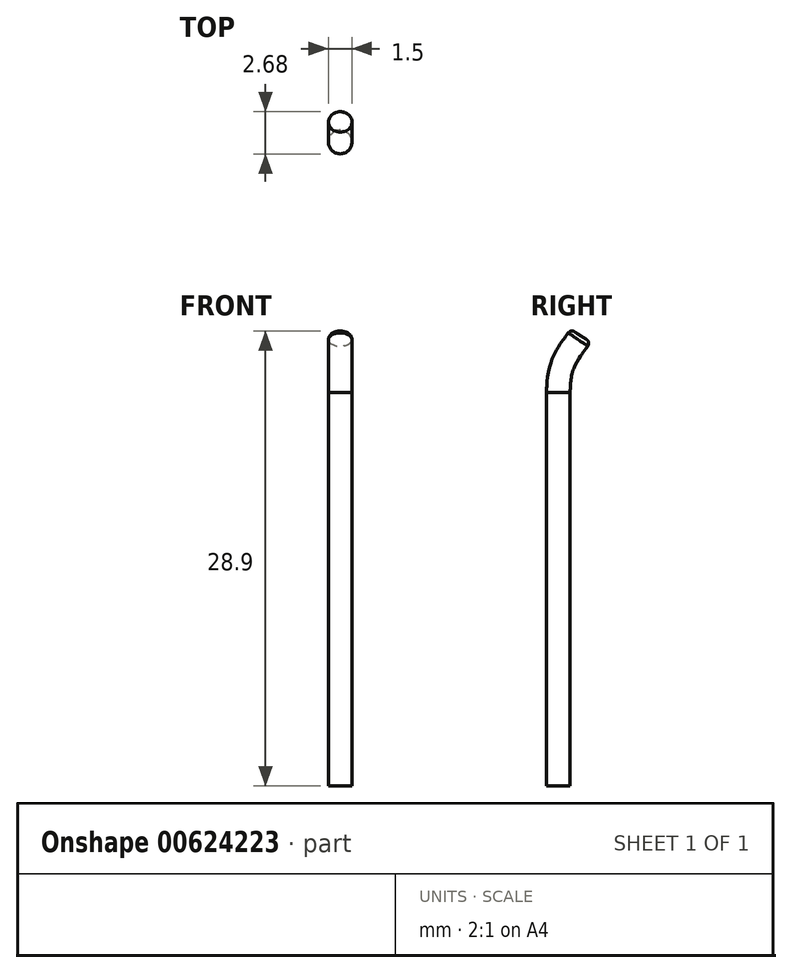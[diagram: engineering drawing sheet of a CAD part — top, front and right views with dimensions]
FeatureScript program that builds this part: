
annotation { "Feature Type Name" : "Feature", "Feature Type Description" : "" }
export const myFeature = defineFeature(function(context is Context, id is Id, definition is map)
    precondition{}
    {
        {
            var Q0;
            Q0=qCreatedBy(makeId("Top.planeOp"),FACE);
            var sketch = newSketch(context, id + "F0", { "sketchPlane" : qUnion([Q0])});
            skCircle(sketch, "E0", {"center": v(0, 0) * mm, "radius": 0.75 * mm});
            skSolve(sketch);
        }
        {
            var Q0;
            Q0=makeQuery(id+"F0.imprint","IMPRINT",FACE,{"disambiguationData":[TD([[makeQuery(id+"F0.imprint","IMPRINT",EDGE,{"derivedFrom":sQuery(id+"F0.wireOp",EDGE,"E0")}),1.0]])]});
            extrude(context, id + "F1", {"entities" : qUnion([Q0]), "depth" : 25 * mm, "offsetDistance" : 25 * mm});
        }
        {
            var Q0;
            Q0=makeQuery(id+"F1.opExtrude","CAP_FACE",FACE,{"disambiguationData":[OSD([sQuery(id+"F0.wireOp",EDGE,"E0")])],"isStart":false});
            cPlane(context, id + "F2", {"entities" : qUnion([Q0]), "cplaneType" : CPlaneType.OFFSET, "offset" : 0 * mm, "width" : 150 * mm, "height" : 150 * mm});
        }
        {
            var Q0;
            Q0=qCreatedBy(makeId("Right.planeOp"),FACE);
            cPlane(context, id + "F3", {"entities" : qUnion([Q0]), "cplaneType" : CPlaneType.OFFSET, "offset" : 0 * mm, "width" : 150 * mm, "height" : 150 * mm});
        }
        {
            var Q0;
            Q0=qCreatedBy(id+"F3.planeOp",FACE);
            var sketch = newSketch(context, id + "F4", { "sketchPlane" : qUnion([Q0])});
            skFitSpline(sketch, "E1", {"points": [v(0, 25) * mm, v(0.3, 26.8) * mm, v(1.28, 28.4) * mm, v(1.43, 28.6) * mm], "startDerivative": vector(0.2, 3.72) * mm, "endDerivative": vector(0.66, 0.93) * mm});
            skSolve(sketch);
        }
        {
            var Q0;
            Q0=qCreatedBy(id+"F2.planeOp",FACE);
            var sketch = newSketch(context, id + "F5", { "sketchPlane" : qUnion([Q0])});
            skCircle(sketch, "E2", {"center": v(0, 0) * mm, "radius": 0.75 * mm});
            skSolve(sketch);
        }
        {
            var Q0;
            Q0=makeQuery(id+"F5.imprint","IMPRINT",FACE,{"disambiguationData":[TD([[makeQuery(id+"F5.imprint","IMPRINT",EDGE,{"derivedFrom":sQuery(id+"F5.wireOp",EDGE,"E2")}),1.0]])]});
            var Q1;
            Q1=sQuery(id+"F4.wireOp",EDGE,"E1");
            sweep(context, id + "F6", {"operationType" : NewBodyOperationType.ADD, "profiles" : qUnion([Q0]), "path" : qUnion([Q1])});
        }
        {
            var Q0;
            Q0=makeQuery(id+"F6.opSweep","CAP_EDGE",EDGE,{"disambiguationData":[OSD([sQuery(id+"F4.wireOp",VERTEX,"E1.end"),sQuery(id+"F5.wireOp",EDGE,"E2")])],"isStart":false});
            fillet(context, id + "F7", {"entities" : qUnion([Q0]), "radius" : 0.3 * mm, "tangentPropagation" : true, "allowEdgeOverflow" : false});
        }
    });
